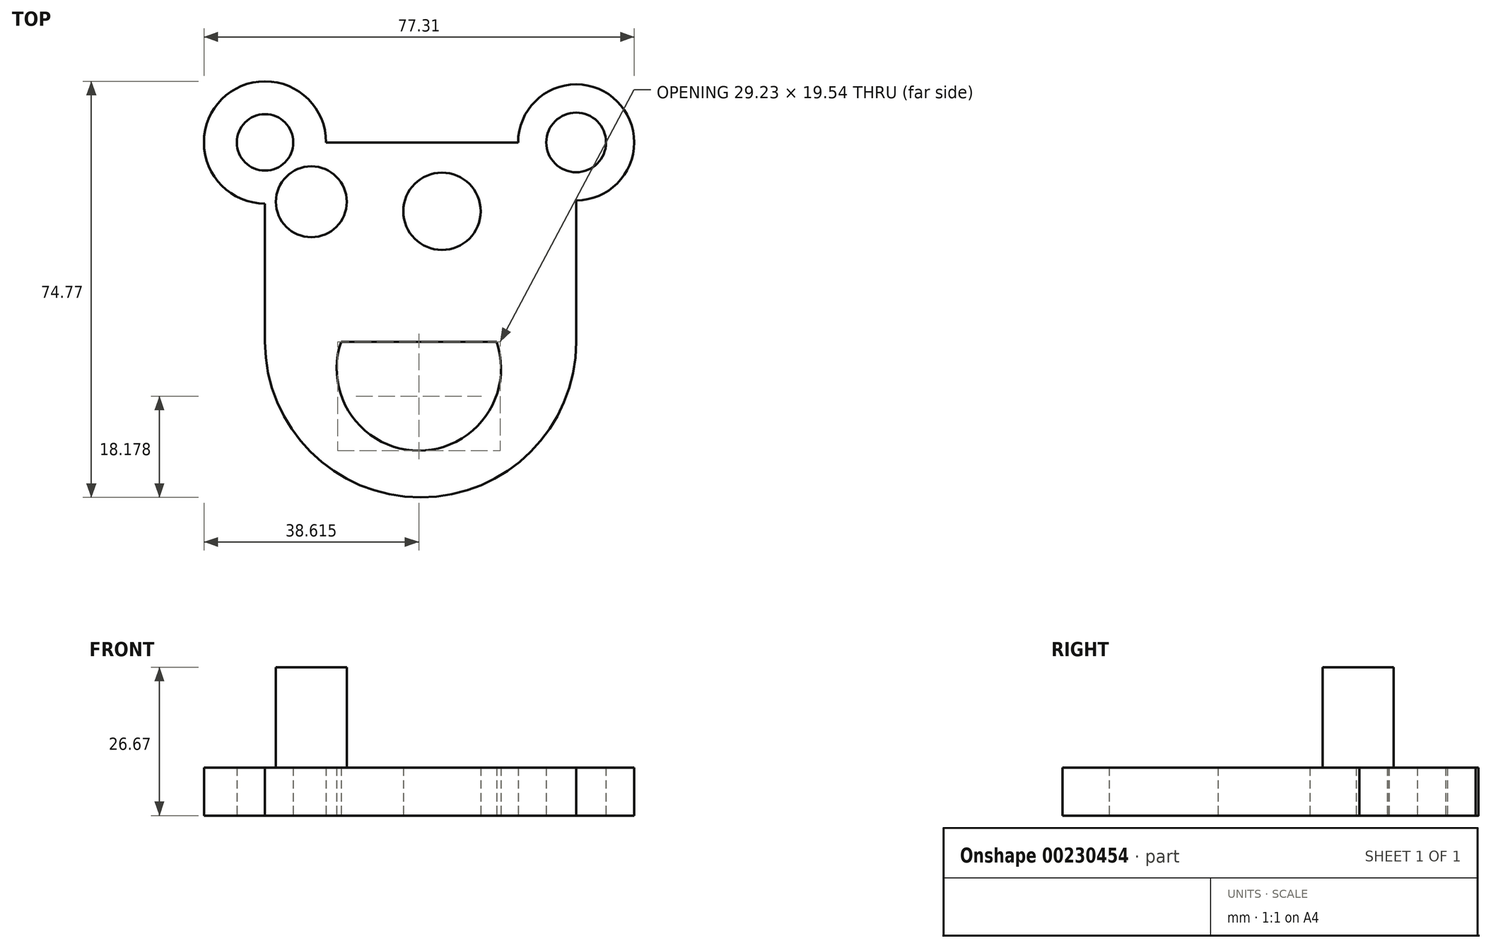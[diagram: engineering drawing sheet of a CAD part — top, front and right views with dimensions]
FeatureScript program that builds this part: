
annotation { "Feature Type Name" : "Feature", "Feature Type Description" : "" }
export const myFeature = defineFeature(function(context is Context, id is Id, definition is map)
    precondition{}
    {
        {
            var Q0;
            Q0=qCreatedBy(makeId("Top.planeOp"),FACE);
            var sketch = newSketch(context, id + "F0", { "sketchPlane" : qUnion([Q0])});
            skLineSegment(sketch, "E0.top", {"start": v(-18.35, -23.47) * mm, "end": v(37.55, -23.47) * mm});
            skLineSegment(sketch, "E0.left", {"start": v(-18.35, 1.4) * mm, "end": v(-18.35, -23.47) * mm});
            skLineSegment(sketch, "E0.right", {"start": v(37.55, 1.95) * mm, "end": v(37.55, -23.47) * mm});
            skCircle(sketch, "E1", {"center": v(-18.35, 12.37) * mm, "radius": 10.98 * mm});
            skCircle(sketch, "E2", {"center": v(37.55, 12.37) * mm, "radius": 10.43 * mm});
            skArc(sketch, "E3", {"start": v(-18.35, -23.47) * mm, "mid": v(9.6, -51.42) * mm, "end": v(37.55, -23.47) * mm});
            skArc(sketch, "E4", {"start": v(-4.7, -23.47) * mm, "mid": v(9.29, -43.01) * mm, "end": v(23.26, -23.47) * mm});
            skCircle(sketch, "E5", {"center": v(13.45, 0) * mm, "radius": 6.95 * mm});
            skCircle(sketch, "E6", {"center": v(37.55, 12.37) * mm, "radius": 5.37 * mm});
            skCircle(sketch, "E7", {"center": v(-18.35, 12.37) * mm, "radius": 5.07 * mm});
            skLineSegment(sketch, "E8.trimOffspring", {"start": v(-7.37, 12.37) * mm, "end": v(27.13, 12.37) * mm});
            skPoint(sketch, "E9.start.orphan", {"position": v(0, -39.73) * mm});
            skSolve(sketch);
        }
        {
            var Q0;
            Q0 = qSketchRegion(id + "F0", true);
            extrude(context, id + "F1", {"entities" : qUnion([Q0]), "depth" : 8.64 * mm});
        }
        {
            var Q0;
            Q0=qCreatedBy(makeId("Top.planeOp"),FACE);
            var sketch = newSketch(context, id + "F2", { "sketchPlane" : qUnion([Q0])});
            skCircle(sketch, "E10", {"center": v(-10.03, 1.7) * mm, "radius": 6.37 * mm});
            skSolve(sketch);
        }
        {
            var Q0;
            Q0 = qSketchRegion(id + "F2", true);
            extrude(context, id + "F3", {"entities" : qUnion([Q0]), "operationType" : NewBodyOperationType.ADD, "depth" : 26.67 * mm});
        }
    });
